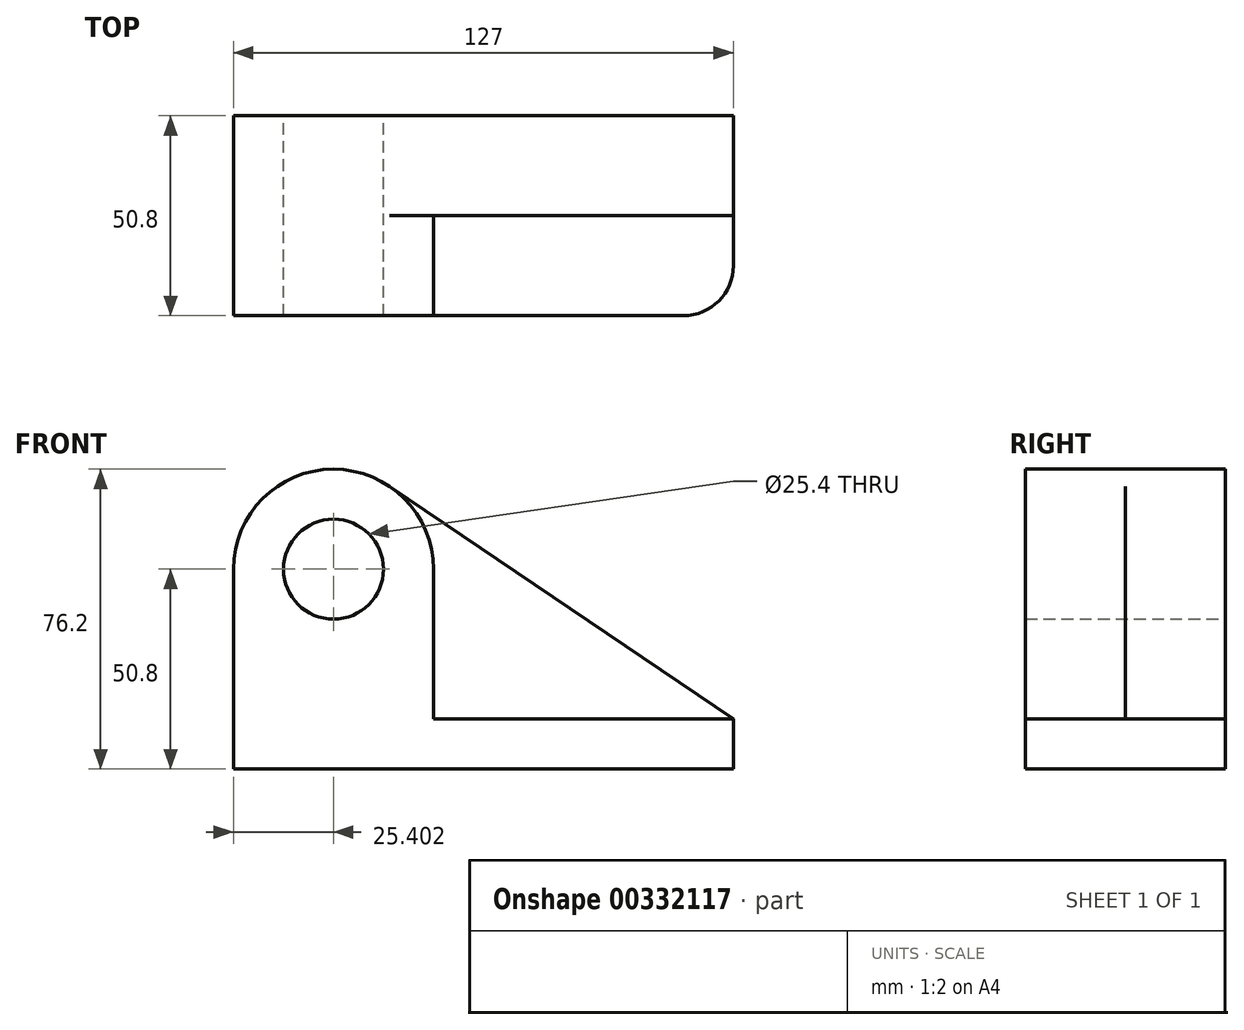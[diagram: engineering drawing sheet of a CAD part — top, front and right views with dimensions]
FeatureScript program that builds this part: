
annotation { "Feature Type Name" : "Feature", "Feature Type Description" : "" }
export const myFeature = defineFeature(function(context is Context, id is Id, definition is map)
    precondition{}
    {
        {
            var Q0;
            Q0=qCreatedBy(makeId("Front.planeOp"),FACE);
            var sketch = newSketch(context, id + "F0", { "sketchPlane" : qUnion([Q0])});
            skCircle(sketch, "E0", {"center": v(-58.89, 34.07) * mm, "radius": 12.7 * mm});
            skArc(sketch, "E1", {"start": v(-44.65, 55.1) * mm, "mid": v(-70.8, 56.5) * mm, "end": v(-84.29, 34.07) * mm});
            skLineSegment(sketch, "E2", {"start": v(-84.29, 34.07) * mm, "end": v(-84.29, -16.73) * mm});
            skLineSegment(sketch, "E3", {"start": v(-84.29, -16.73) * mm, "end": v(42.71, -16.73) * mm});
            skLineSegment(sketch, "E4", {"start": v(42.71, -16.73) * mm, "end": v(42.71, -4.03) * mm});
            skLineSegment(sketch, "E5", {"start": v(42.71, -4.03) * mm, "end": v(-44.65, 55.1) * mm});
            skSolve(sketch);
        }
        {
            var Q0;
            Q0=makeQuery(id+"F0.imprint","IMPRINT",FACE,{"disambiguationData":[TD([[makeQuery(id+"F0.imprint","IMPRINT",EDGE,{"derivedFrom":sQuery(id+"F0.wireOp",EDGE,"E0")}),-1.0]])]});
            extrude(context, id + "F1", {"entities" : qUnion([Q0]), "depth" : 25.4 * mm});
        }
        {
            var Q0;
            Q0=makeQuery(id+"F1.opExtrude","CAP_FACE",FACE,{"disambiguationData":[OSD([sQuery(id+"F0.wireOp",EDGE,"E0"),sQuery(id+"F0.wireOp",EDGE,"E1"),sQuery(id+"F0.wireOp",EDGE,"E2"),sQuery(id+"F0.wireOp",EDGE,"E3"),sQuery(id+"F0.wireOp",EDGE,"E4"),sQuery(id+"F0.wireOp",EDGE,"E5")])],"isStart":false});
            var sketch = newSketch(context, id + "F2", { "sketchPlane" : qUnion([Q0])});
            skArc(sketch, "E6", {"start": v(-33.49, 34.07) * mm, "mid": v(-58.89, 59.47) * mm, "end": v(-84.29, 34.07) * mm});
            skLineSegment(sketch, "E7.bottom", {"start": v(42.71, -4.03) * mm, "end": v(-33.49, -4.03) * mm});
            skLineSegment(sketch, "E7.top", {"start": v(42.71, -16.73) * mm, "end": v(-84.29, -16.73) * mm});
            skLineSegment(sketch, "E7.left", {"start": v(42.71, -4.03) * mm, "end": v(42.71, -16.73) * mm});
            skLineSegment(sketch, "E7.right", {"start": v(-84.29, -4.03) * mm, "end": v(-84.29, -16.73) * mm});
            skLineSegment(sketch, "E8", {"start": v(-84.29, 34.07) * mm, "end": v(-84.29, -4.03) * mm});
            skLineSegment(sketch, "E9", {"start": v(-33.49, 34.07) * mm, "end": v(-33.49, -4.03) * mm});
            skSolve(sketch);
        }
        {
            var Q0;
            Q0=makeQuery(id+"F2.imprint","IMPRINT",FACE,{"disambiguationData":[TD([[makeQuery(id+"F2.imprint","IMPRINT",EDGE,{"derivedFrom":sQuery(id+"F2.wireOp",EDGE,"E7.bottom")}),1.0]])]});
            extrude(context, id + "F3", {"entities" : qUnion([Q0]), "operationType" : NewBodyOperationType.ADD, "depth" : 25.4 * mm});
        }
        {
            var Q0;
            Q0=makeQuery(id+"F3.opExtrude","CAP_EDGE",EDGE,{"disambiguationData":[OSD([sQuery(id+"F2.wireOp",EDGE,"E7.left")])],"isStart":false});
            fillet(context, id + "F4", {"entities" : qUnion([Q0]), "radius" : 12.7 * mm, "tangentPropagation" : true, "allowEdgeOverflow" : false});
        }
    });
